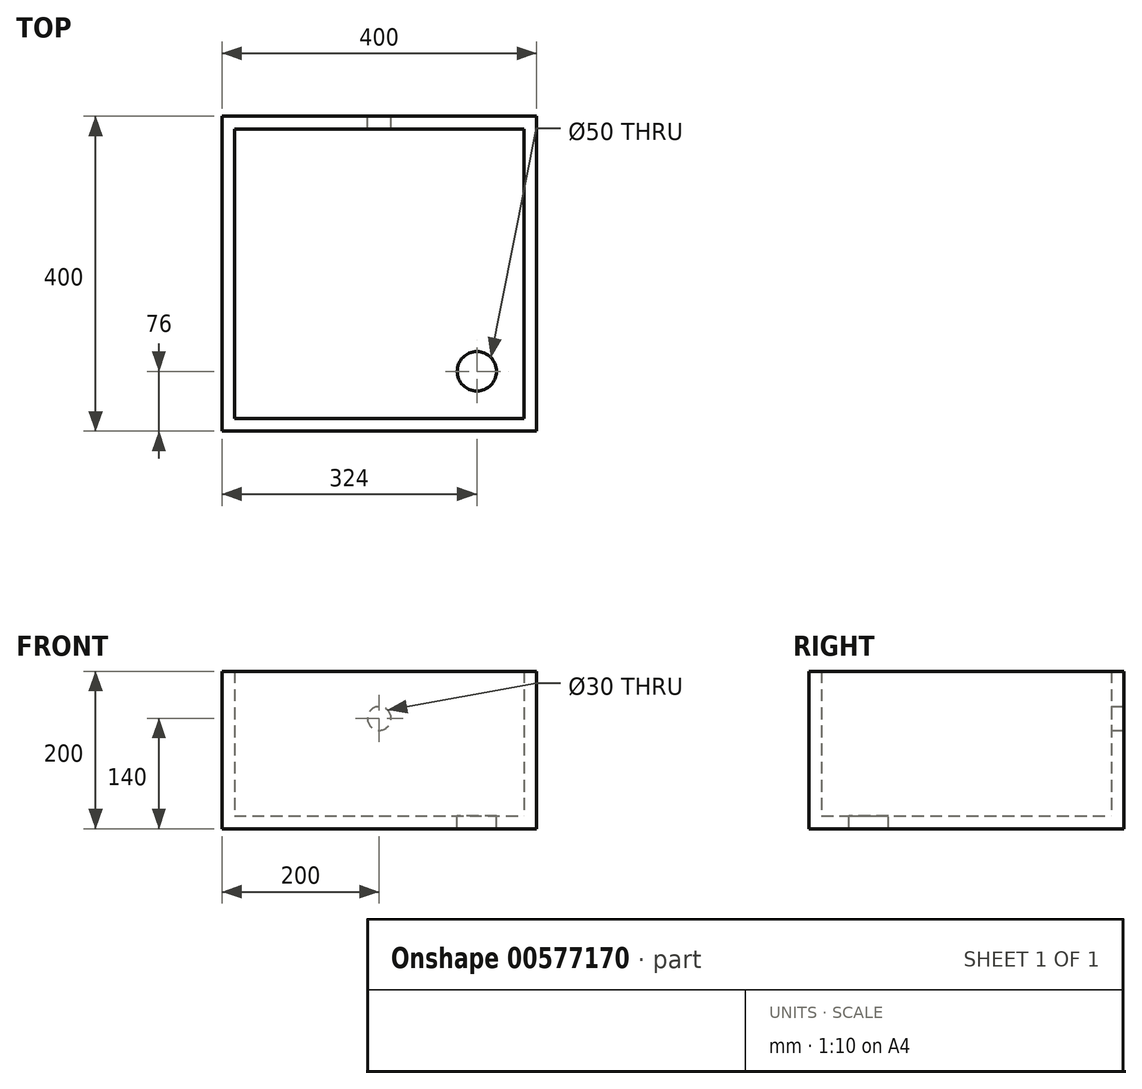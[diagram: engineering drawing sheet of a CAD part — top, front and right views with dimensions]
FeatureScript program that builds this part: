
annotation { "Feature Type Name" : "Feature", "Feature Type Description" : "" }
export const myFeature = defineFeature(function(context is Context, id is Id, definition is map)
    precondition{}
    {
        {
            var Q0;
            Q0=qCreatedBy(makeId("Front.planeOp"),FACE);
            var sketch = newSketch(context, id + "F0", { "sketchPlane" : qUnion([Q0])});
            skLineSegment(sketch, "E0.bottom", {"start": v(-200, 100) * mm, "end": v(200, 100) * mm});
            skLineSegment(sketch, "E0.top", {"start": v(-200, -100) * mm, "end": v(200, -100) * mm});
            skLineSegment(sketch, "E0.left", {"start": v(-200, 100) * mm, "end": v(-200, -100) * mm});
            skLineSegment(sketch, "E0.right", {"start": v(200, 100) * mm, "end": v(200, -100) * mm});
            skPoint(sketch, "E0.middle", {"position": v(0, 0) * mm});
            skPoint(sketch, "E1", {"position": v(0, 40) * mm});
            skSolve(sketch);
        }
        {
            var Q0;
            Q0=makeQuery(id+"F0.imprint","IMPRINT",FACE,{"disambiguationData":[TD([[makeQuery(id+"F0.imprint","IMPRINT",EDGE,{"derivedFrom":sQuery(id+"F0.wireOp",EDGE,"E0.bottom")}),-1.0]])]});
            extrude(context, id + "F1", {"entities" : qUnion([Q0]), "depth" : 400 * mm, "offsetDistance" : 25 * mm});
        }
        {
            var Q0;
            Q0=makeQuery(id+"F1.opExtrude","SWEPT_FACE",FACE,{"disambiguationData":[OSD([sQuery(id+"F0.wireOp",EDGE,"E0.bottom")])]});
            shell(context, id + "F2", {"entities" : qUnion([Q0]), "thickness" : 16 * mm});
        }
        {
            var Q0;
            Q0=sQuery(id+"F0.wireOp",VERTEX,"E1");
            var Q1;
            Q1=makeQuery(id+"F1.opExtrude","SWEPT_BODY",BODY,{"disambiguationData":[OSD([sQuery(id+"F0.wireOp",EDGE,"E0.bottom"),sQuery(id+"F0.wireOp",EDGE,"E0.top"),sQuery(id+"F0.wireOp",EDGE,"E0.left"),sQuery(id+"F0.wireOp",EDGE,"E0.right")])]});
            hole(context, id + "F3", {"style" : HoleStyle.SIMPLE, "endStyle" : HoleEndStyle.BLIND, "oppositeDirection" : true, "holeDiameter" : 30 * mm, "majorDiameter" : 5 * mm, "holeDepth" : 16 * mm, "isTappedThrough" : true, "tappedDepth" : 12 * mm, "tapClearance" : 3, "locations" : qUnion([Q0]), "scope" : qUnion([Q1])});
        }
        {
            var Q0;
            Q0=makeQuery(id+"F2.opShell","OFFSET_FACE",FACE,{"disambiguationData":[OSD([sQuery(id+"F0.wireOp",EDGE,"E0.top")])]});
            var sketch = newSketch(context, id + "F4", { "sketchPlane" : qUnion([Q0])});
            skPoint(sketch, "E2", {"position": v(124, -324) * mm});
            skSolve(sketch);
        }
        {
            var Q0;
            Q0=sQuery(id+"F4.wireOp",VERTEX,"E2");
            var Q1;
            Q1=makeQuery(id+"F1.opExtrude","SWEPT_BODY",BODY,{"disambiguationData":[OSD([sQuery(id+"F0.wireOp",EDGE,"E0.bottom"),sQuery(id+"F0.wireOp",EDGE,"E0.top"),sQuery(id+"F0.wireOp",EDGE,"E0.left"),sQuery(id+"F0.wireOp",EDGE,"E0.right")])]});
            hole(context, id + "F5", {"style" : HoleStyle.SIMPLE, "endStyle" : HoleEndStyle.THROUGH, "holeDiameter" : 50 * mm, "majorDiameter" : 5 * mm, "isTappedThrough" : true, "tappedDepth" : 12 * mm, "tapClearance" : 3, "locations" : qUnion([Q0]), "scope" : qUnion([Q1])});
        }
    });
